# Revit family: GO_undercabinets
name_source: partatom
category: Furniture
units: mm (PartAtom-declared; Revit-internal decimal feet)

## family parameters
Always vertical = Yes
Cut with Voids When Loaded = No
OmniClass Number = 23.40.20.00
OmniClass Title = General Furniture and Specialties
Room Calculation Point = No
Shared = No
Work Plane-Based = No

## types (12) — shared parameters
ETIM = EC011382
Manufacturer = Hafa Bathroom Group AB
Material body = Moisture resistant chip board E1 certified
Material front = Moisure resistant MDF FSC and  E1 certified
Model = Go under cabinets
Surface finish = Lacquered
Svulsthöjd = 752 mm
URL = www.hafa.se

## per-type parameters (varying)
| type | Article number | Depth | Finish | GTIN | Width |
| Go 600 white matt | 1580010 | 450 mm  [stored 1.47638 ft] | NCS S 0300-N 20% gloss white matt | 7330027103532 | 600 mm  [stored 1.9685 ft] |
| Go 800 white matt | 1580020 | 450 mm  [stored 1.47638 ft] | NCS S 0300-N 20% gloss white matt | 7330027103556 | 800 mm  [stored 2.62467 ft] |
| Go 1000 white matt | 1580030 | 450 mm  [stored 1.47638 ft] | NCS S 0300-N 20% gloss white matt | 7330027103570 | 1000 mm  [stored 3.28084 ft] |
| Go 600 black matt | 1580011 | 450 mm  [stored 1.47638 ft] | NCS S 8000-N 10% gloss anthracite | 7330027103549 | 600 mm  [stored 1.9685 ft] |
| Go 800 black matt | 1580021 | 450 mm  [stored 1.47638 ft] | NCS S 9000-N 10% gloss black matt | 7330027103563 | 800 mm  [stored 2.62467 ft] |
| Go 1000 black matt | 1580031 | 450 mm  [stored 1.47638 ft] | NCS S 9000-N 10% gloss black matt | 7330027103587 | 1000 mm  [stored 3.28084 ft] |
| Go 600 white highgloss | 1580012 | 450 mm  [stored 1.47638 ft] | NCS S 0300-N 90% gloss white highgloss | 7330027096827 | 600 mm  [stored 1.9685 ft] |
| Go 800 white highgloss | 1580022 | 450 mm  [stored 1.47638 ft] | NCS S 0300-N 90% gloss white highgloss | 7330027096834 | 800 mm  [stored 2.62467 ft] |
| Go 1000 white highgloss | 1580032 | 450 mm  [stored 1.47638 ft] | NCS S 0300-N 90% gloss white highgloss | 7330027101941 | 1000 mm  [stored 3.28084 ft] |
| Go 600 compact white matt | 1580101 | 385 mm  [stored 1.26312 ft] | NCS S 0300-N 20% gloss white matt | 7330027096797 | 600 mm  [stored 1.9685 ft] |
| Go 600 compact black matt | 1580100 | 385 mm  [stored 1.26312 ft] | NCS S 9000-N 10% gloss black matt | 7330027096780 | 600 mm  [stored 1.9685 ft] |
| Go 600 compact white highgloss | 1580102 | 385 mm  [stored 1.26312 ft] | NCS S 0300-N 90% gloss white highgloss | 7330027096803 | 600 mm  [stored 1.9685 ft] |

note: [stored X ft] marks values corroborated as IEEE doubles in the binary element streams (Revit-internal decimal feet)

## geometry (parser evidence)
native form markers: Sweep x9
no freeform markers — native parametric forms only
